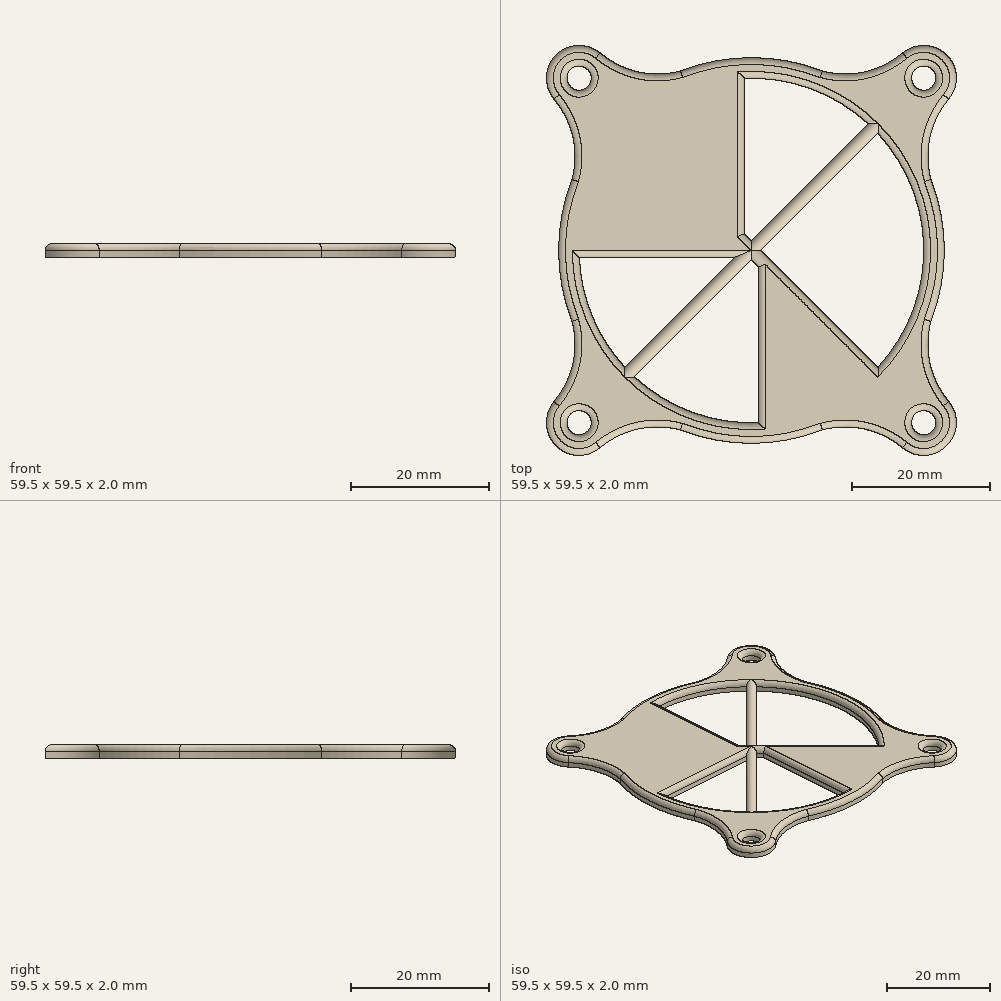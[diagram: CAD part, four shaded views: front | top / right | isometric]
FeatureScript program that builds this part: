
annotation { "Feature Type Name" : "Feature", "Feature Type Description" : "" }
export const myFeature = defineFeature(function(context is Context, id is Id, definition is map)
    precondition{}
    {
        {
            var Q0;
            Q0=qCreatedBy(makeId("Top.planeOp"),FACE);
            var sketch = newSketch(context, id + "F0", { "sketchPlane" : qUnion([Q0])});
            skCircle(sketch, "E0", {"center": v(0, 0) * mm, "radius": 25 * mm});
            skCircle(sketch, "E1.0", {"center": v(0, 0) * mm, "radius": 28 * mm});
            skLineSegment(sketch, "E2.bottom", {"start": v(25, 25) * mm, "end": v(-25, 25) * mm, "construction": true});
            skLineSegment(sketch, "E2.top", {"start": v(25, -25) * mm, "end": v(-25, -25) * mm, "construction": true});
            skLineSegment(sketch, "E2.left", {"start": v(25, 25) * mm, "end": v(25, -25) * mm, "construction": true});
            skLineSegment(sketch, "E2.right", {"start": v(-25, 25) * mm, "end": v(-25, -25) * mm, "construction": true});
            skCircle(sketch, "E3", {"center": v(-25, 25) * mm, "radius": 1.75 * mm});
            skCircle(sketch, "E4", {"center": v(25, 25) * mm, "radius": 1.75 * mm});
            skCircle(sketch, "E5", {"center": v(25, -25) * mm, "radius": 1.75 * mm});
            skCircle(sketch, "E6", {"center": v(-25, -25) * mm, "radius": 1.75 * mm});
            skCircle(sketch, "E7.0", {"center": v(-25, 25) * mm, "radius": 4.75 * mm});
            skCircle(sketch, "E8.0", {"center": v(25, 25) * mm, "radius": 4.75 * mm});
            skCircle(sketch, "E9.0", {"center": v(25, -25) * mm, "radius": 4.75 * mm});
            skCircle(sketch, "E10.0", {"center": v(-25, -25) * mm, "radius": 4.75 * mm});
            skLineSegment(sketch, "E11", {"start": v(0, 36.28) * mm, "end": v(0, -46.87) * mm, "construction": true});
            skLineSegment(sketch, "E12", {"start": v(-54.76, 0) * mm, "end": v(48.87, 0) * mm, "construction": true});
            skArc(sketch, "E13", {"start": v(26.04, -10.28) * mm, "mid": v(25.92, -16.43) * mm, "end": v(28.64, -21.95) * mm});
            skLineSegment(sketch, "E14", {"start": v(25, -25) * mm, "end": v(-25, 25) * mm, "construction": true});
            skArc(sketch, "E15.MirrorCS", {"start": v(10.28, -26.04) * mm, "mid": v(16.43, -25.92) * mm, "end": v(21.95, -28.64) * mm});
            skArc(sketch, "E16.MirrorCS", {"start": v(-26.04, -10.28) * mm, "mid": v(-25.92, -16.43) * mm, "end": v(-28.64, -21.95) * mm});
            skArc(sketch, "E17.MirrorCS", {"start": v(-10.28, -26.04) * mm, "mid": v(-16.43, -25.92) * mm, "end": v(-21.95, -28.64) * mm});
            skArc(sketch, "E18.MirrorCS", {"start": v(-26.04, 10.28) * mm, "mid": v(-25.92, 16.43) * mm, "end": v(-28.64, 21.95) * mm});
            skArc(sketch, "E19.MirrorCS", {"start": v(-10.28, 26.04) * mm, "mid": v(-16.43, 25.92) * mm, "end": v(-21.95, 28.64) * mm});
            skArc(sketch, "E20.MirrorCS", {"start": v(10.28, 26.04) * mm, "mid": v(16.43, 25.92) * mm, "end": v(21.95, 28.64) * mm});
            skArc(sketch, "E21.MirrorCS", {"start": v(26.04, 10.28) * mm, "mid": v(25.92, 16.43) * mm, "end": v(28.64, 21.95) * mm});
            skLineSegment(sketch, "E22", {"start": v(-24.98, -1) * mm, "end": v(25, -1) * mm});
            skLineSegment(sketch, "E23.MirrorCS", {"start": v(-24.98, 1) * mm, "end": v(25, 1) * mm});
            skLineSegment(sketch, "E24", {"start": v(1, -25) * mm, "end": v(1, 24.98) * mm});
            skLineSegment(sketch, "E25.MirrorCS", {"start": v(-1, -25) * mm, "end": v(-1, 24.98) * mm});
            skLineSegment(sketch, "E26", {"start": v(25, 25) * mm, "end": v(-25, -25) * mm, "construction": true});
            skLineSegment(sketch, "E27", {"start": v(16.96, 18.37) * mm, "end": v(-18.37, -16.96) * mm});
            skLineSegment(sketch, "E28.MirrorCS", {"start": v(18.37, 16.96) * mm, "end": v(-16.96, -18.37) * mm});
            skLineSegment(sketch, "E29", {"start": v(-18.37, 16.96) * mm, "end": v(16.96, -18.37) * mm});
            skLineSegment(sketch, "E30.MirrorCS", {"start": v(-16.96, 18.37) * mm, "end": v(18.37, -16.96) * mm});
            skSolve(sketch);
        }
        {
            var Q0;
            Q0 = qSketchRegion(id + "F0", true);
            var Q1;
            {var subQ0=sQuery(id+"F0.wireOp",EDGE,"E29");var subQ1=sQuery(id+"F0.wireOp",EDGE,"E0");var subQ2=makeQuery(id+"F0.imprint","INTERSECT",VERTEX,{"disambiguationData":[OD(0.0)],"derivedFrom":[subQ1,subQ0]});Q1=makeQuery(id+"F0.imprint","IMPRINT",FACE,{"disambiguationData":[TD([[makeQuery(id+"F0.imprint","IMPRINT",EDGE,{"disambiguationData":[TD([[subQ2,1.0]])],"derivedFrom":subQ1}),1.0]])]});}
            var Q2;
            {var subQ1=sQuery(id+"F0.wireOp",EDGE,"E0");var subQ5=sQuery(id+"F0.wireOp",EDGE,"E22");var subQ6=makeQuery(id+"F0.imprint","INTERSECT",VERTEX,{"disambiguationData":[OD(0.0)],"derivedFrom":[subQ1,subQ5]});Q2=makeQuery(id+"F0.imprint","IMPRINT",FACE,{"disambiguationData":[TD([[makeQuery(id+"F0.imprint","IMPRINT",EDGE,{"disambiguationData":[TD([[subQ6,1.0]])],"derivedFrom":subQ1}),1.0]])]});}
            var Q3;
            {var subQ0=sQuery(id+"F0.wireOp",EDGE,"E27");var subQ1=sQuery(id+"F0.wireOp",EDGE,"E0");var subQ2=makeQuery(id+"F0.imprint","INTERSECT",VERTEX,{"disambiguationData":[OD(0.0)],"derivedFrom":[subQ1,subQ0]});Q3=makeQuery(id+"F0.imprint","IMPRINT",FACE,{"disambiguationData":[TD([[makeQuery(id+"F0.imprint","IMPRINT",EDGE,{"disambiguationData":[TD([[subQ2,1.0]])],"derivedFrom":subQ1}),1.0]])]});}
            var Q4;
            {var subQ1=sQuery(id+"F0.wireOp",EDGE,"E0");var subQ5=sQuery(id+"F0.wireOp",EDGE,"E24");var subQ6=makeQuery(id+"F0.imprint","INTERSECT",VERTEX,{"disambiguationData":[OD(0.0)],"derivedFrom":[subQ1,subQ5]});Q4=makeQuery(id+"F0.imprint","IMPRINT",FACE,{"disambiguationData":[TD([[makeQuery(id+"F0.imprint","IMPRINT",EDGE,{"disambiguationData":[TD([[subQ6,-1.0]])],"derivedFrom":subQ1}),1.0]])]});}
            var Q5;
            {var subQ0=sQuery(id+"F0.wireOp",EDGE,"E27");var subQ1=sQuery(id+"F0.wireOp",EDGE,"E0");var subQ2=makeQuery(id+"F0.imprint","INTERSECT",VERTEX,{"disambiguationData":[OD(1.0)],"derivedFrom":[subQ1,subQ0]});Q5=makeQuery(id+"F0.imprint","IMPRINT",FACE,{"disambiguationData":[TD([[makeQuery(id+"F0.imprint","IMPRINT",EDGE,{"disambiguationData":[TD([[subQ2,-1.0]])],"derivedFrom":subQ1}),1.0]])]});}
            var Q6;
            {var subQ1=sQuery(id+"F0.wireOp",EDGE,"E25.MirrorCS");var subQ5=sQuery(id+"F0.wireOp",EDGE,"E0");var subQ6=makeQuery(id+"F0.imprint","INTERSECT",VERTEX,{"disambiguationData":[OD(1.0)],"derivedFrom":[subQ5,subQ1]});Q6=makeQuery(id+"F0.imprint","IMPRINT",FACE,{"disambiguationData":[TD([[makeQuery(id+"F0.imprint","IMPRINT",EDGE,{"disambiguationData":[TD([[subQ6,-1.0]])],"derivedFrom":subQ5}),1.0]])]});}
            var Q7;
            {var subQ0=sQuery(id+"F0.wireOp",EDGE,"E29");var subQ13=sQuery(id+"F0.wireOp",EDGE,"E22");var subQ14=makeQuery(id+"F0.imprint","INTERSECT",VERTEX,{"derivedFrom":[subQ13,subQ0]});Q7=makeQuery(id+"F0.imprint","IMPRINT",FACE,{"disambiguationData":[TD([[makeQuery(id+"F0.imprint","IMPRINT",EDGE,{"disambiguationData":[TD([[subQ14,-1.0]])],"derivedFrom":subQ13}),1.0]])]});}
            var Q8;
            {var subQ0=sQuery(id+"F0.wireOp",EDGE,"E29");var subQ1=sQuery(id+"F0.wireOp",EDGE,"E0");var subQ2=makeQuery(id+"F0.imprint","INTERSECT",VERTEX,{"disambiguationData":[OD(1.0)],"derivedFrom":[subQ1,subQ0]});Q8=makeQuery(id+"F0.imprint","IMPRINT",FACE,{"disambiguationData":[TD([[makeQuery(id+"F0.imprint","IMPRINT",EDGE,{"disambiguationData":[TD([[subQ2,-1.0]])],"derivedFrom":subQ1}),1.0]])]});}
            var Q9;
            {var subQ0=sQuery(id+"F0.wireOp",EDGE,"E23.MirrorCS");var subQ1=sQuery(id+"F0.wireOp",EDGE,"E0");var subQ2=makeQuery(id+"F0.imprint","INTERSECT",VERTEX,{"disambiguationData":[OD(1.0)],"derivedFrom":[subQ1,subQ0]});Q9=makeQuery(id+"F0.imprint","IMPRINT",FACE,{"disambiguationData":[TD([[makeQuery(id+"F0.imprint","IMPRINT",EDGE,{"disambiguationData":[TD([[subQ2,1.0]])],"derivedFrom":subQ1}),1.0]])]});}
            var Q10;
            {var subQ0=sQuery(id+"F0.wireOp",EDGE,"E24");var subQ1=sQuery(id+"F0.wireOp",EDGE,"E22");var subQ2=makeQuery(id+"F0.imprint","INTERSECT",VERTEX,{"derivedFrom":[subQ1,subQ0]});Q10=makeQuery(id+"F0.imprint","IMPRINT",FACE,{"disambiguationData":[TD([[makeQuery(id+"F0.imprint","IMPRINT",EDGE,{"disambiguationData":[TD([[subQ2,-1.0]])],"derivedFrom":subQ1}),1.0]])]});}
            var Q11;
            {var subQ0=sQuery(id+"F0.wireOp",EDGE,"E24");var subQ1=sQuery(id+"F0.wireOp",EDGE,"E23.MirrorCS");var subQ2=makeQuery(id+"F0.imprint","INTERSECT",VERTEX,{"derivedFrom":[subQ1,subQ0]});Q11=makeQuery(id+"F0.imprint","IMPRINT",FACE,{"disambiguationData":[TD([[makeQuery(id+"F0.imprint","IMPRINT",EDGE,{"disambiguationData":[TD([[subQ2,-1.0]])],"derivedFrom":subQ1}),-1.0]])]});}
            var Q12;
            {var subQ0=sQuery(id+"F0.wireOp",EDGE,"E25.MirrorCS");var subQ1=sQuery(id+"F0.wireOp",EDGE,"E23.MirrorCS");var subQ2=makeQuery(id+"F0.imprint","INTERSECT",VERTEX,{"derivedFrom":[subQ1,subQ0]});Q12=makeQuery(id+"F0.imprint","IMPRINT",FACE,{"disambiguationData":[TD([[makeQuery(id+"F0.imprint","IMPRINT",EDGE,{"disambiguationData":[TD([[subQ2,-1.0]])],"derivedFrom":subQ1}),1.0]])]});}
            var Q13;
            {var subQ0=sQuery(id+"F0.wireOp",EDGE,"E29");var subQ1=sQuery(id+"F0.wireOp",EDGE,"E23.MirrorCS");var subQ2=makeQuery(id+"F0.imprint","INTERSECT",VERTEX,{"derivedFrom":[subQ1,subQ0]});Q13=makeQuery(id+"F0.imprint","IMPRINT",FACE,{"disambiguationData":[TD([[makeQuery(id+"F0.imprint","IMPRINT",EDGE,{"disambiguationData":[TD([[subQ2,-1.0]])],"derivedFrom":subQ1}),-1.0]])]});}
            var Q14;
            {var subQ0=sQuery(id+"F0.wireOp",EDGE,"E30.MirrorCS");var subQ1=sQuery(id+"F0.wireOp",EDGE,"E23.MirrorCS");var subQ2=makeQuery(id+"F0.imprint","INTERSECT",VERTEX,{"derivedFrom":[subQ1,subQ0]});Q14=makeQuery(id+"F0.imprint","IMPRINT",FACE,{"disambiguationData":[TD([[makeQuery(id+"F0.imprint","IMPRINT",EDGE,{"disambiguationData":[TD([[subQ2,-1.0]])],"derivedFrom":subQ1}),1.0]])]});}
            var Q15;
            {var subQ0=sQuery(id+"F0.wireOp",EDGE,"E27");var subQ1=sQuery(id+"F0.wireOp",EDGE,"E22");var subQ2=makeQuery(id+"F0.imprint","INTERSECT",VERTEX,{"derivedFrom":[subQ1,subQ0]});Q15=makeQuery(id+"F0.imprint","IMPRINT",FACE,{"disambiguationData":[TD([[makeQuery(id+"F0.imprint","IMPRINT",EDGE,{"disambiguationData":[TD([[subQ2,-1.0]])],"derivedFrom":subQ1}),1.0]])]});}
            var Q16;
            {var subQ0=sQuery(id+"F0.wireOp",EDGE,"E25.MirrorCS");var subQ1=sQuery(id+"F0.wireOp",EDGE,"E22");var subQ2=makeQuery(id+"F0.imprint","INTERSECT",VERTEX,{"derivedFrom":[subQ1,subQ0]});Q16=makeQuery(id+"F0.imprint","IMPRINT",FACE,{"disambiguationData":[TD([[makeQuery(id+"F0.imprint","IMPRINT",EDGE,{"disambiguationData":[TD([[subQ2,-1.0]])],"derivedFrom":subQ1}),-1.0]])]});}
            var Q17;
            {var subQ0=sQuery(id+"F0.wireOp",EDGE,"E29");var subQ1=sQuery(id+"F0.wireOp",EDGE,"E22");var subQ2=makeQuery(id+"F0.imprint","INTERSECT",VERTEX,{"derivedFrom":[subQ1,subQ0]});Q17=makeQuery(id+"F0.imprint","IMPRINT",FACE,{"disambiguationData":[TD([[makeQuery(id+"F0.imprint","IMPRINT",EDGE,{"disambiguationData":[TD([[subQ2,-1.0]])],"derivedFrom":subQ1}),-1.0]])]});}
            var Q18;
            {var subQ0=sQuery(id+"F0.wireOp",EDGE,"E28.MirrorCS");var subQ1=sQuery(id+"F0.wireOp",EDGE,"E22");var subQ2=makeQuery(id+"F0.imprint","INTERSECT",VERTEX,{"derivedFrom":[subQ1,subQ0]});Q18=makeQuery(id+"F0.imprint","IMPRINT",FACE,{"disambiguationData":[TD([[makeQuery(id+"F0.imprint","IMPRINT",EDGE,{"disambiguationData":[TD([[subQ2,-1.0]])],"derivedFrom":subQ1}),1.0]])]});}
            var Q19;
            {var subQ0=sQuery(id+"F0.wireOp",EDGE,"E28.MirrorCS");var subQ1=sQuery(id+"F0.wireOp",EDGE,"E24");var subQ2=makeQuery(id+"F0.imprint","INTERSECT",VERTEX,{"derivedFrom":[subQ1,subQ0]});Q19=makeQuery(id+"F0.imprint","IMPRINT",FACE,{"disambiguationData":[TD([[makeQuery(id+"F0.imprint","IMPRINT",EDGE,{"disambiguationData":[TD([[subQ2,-1.0]])],"derivedFrom":subQ1}),-1.0]])]});}
            var Q20;
            {var subQ0=sQuery(id+"F0.wireOp",EDGE,"E30.MirrorCS");var subQ1=sQuery(id+"F0.wireOp",EDGE,"E23.MirrorCS");var subQ2=makeQuery(id+"F0.imprint","INTERSECT",VERTEX,{"derivedFrom":[subQ1,subQ0]});Q20=makeQuery(id+"F0.imprint","IMPRINT",FACE,{"disambiguationData":[TD([[makeQuery(id+"F0.imprint","IMPRINT",EDGE,{"disambiguationData":[TD([[subQ2,-1.0]])],"derivedFrom":subQ1}),-1.0]])]});}
            var Q21;
            {var subQ0=sQuery(id+"F0.wireOp",EDGE,"E27");var subQ1=sQuery(id+"F0.wireOp",EDGE,"E23.MirrorCS");var subQ2=makeQuery(id+"F0.imprint","INTERSECT",VERTEX,{"derivedFrom":[subQ1,subQ0]});Q21=makeQuery(id+"F0.imprint","IMPRINT",FACE,{"disambiguationData":[TD([[makeQuery(id+"F0.imprint","IMPRINT",EDGE,{"disambiguationData":[TD([[subQ2,-1.0]])],"derivedFrom":subQ1}),1.0]])]});}
            var Q22;
            {var subQ0=sQuery(id+"F0.wireOp",EDGE,"E25.MirrorCS");var subQ1=sQuery(id+"F0.wireOp",EDGE,"E23.MirrorCS");var subQ2=makeQuery(id+"F0.imprint","INTERSECT",VERTEX,{"derivedFrom":[subQ1,subQ0]});Q22=makeQuery(id+"F0.imprint","IMPRINT",FACE,{"disambiguationData":[TD([[makeQuery(id+"F0.imprint","IMPRINT",EDGE,{"disambiguationData":[TD([[subQ2,-1.0]])],"derivedFrom":subQ1}),-1.0]])]});}
            var Q23;
            {var subQ0=sQuery(id+"F0.wireOp",EDGE,"E29");var subQ1=sQuery(id+"F0.wireOp",EDGE,"E25.MirrorCS");var subQ2=makeQuery(id+"F0.imprint","INTERSECT",VERTEX,{"derivedFrom":[subQ1,subQ0]});Q23=makeQuery(id+"F0.imprint","IMPRINT",FACE,{"disambiguationData":[TD([[makeQuery(id+"F0.imprint","IMPRINT",EDGE,{"disambiguationData":[TD([[subQ2,-1.0]])],"derivedFrom":subQ1}),1.0]])]});}
            var Q24;
            {var subQ0=sQuery(id+"F0.wireOp",EDGE,"E25.MirrorCS");var subQ1=sQuery(id+"F0.wireOp",EDGE,"E22");var subQ2=makeQuery(id+"F0.imprint","INTERSECT",VERTEX,{"derivedFrom":[subQ1,subQ0]});Q24=makeQuery(id+"F0.imprint","IMPRINT",FACE,{"disambiguationData":[TD([[makeQuery(id+"F0.imprint","IMPRINT",EDGE,{"disambiguationData":[TD([[subQ2,-1.0]])],"derivedFrom":subQ1}),1.0]])]});}
            var Q25;
            {var subQ0=sQuery(id+"F0.wireOp",EDGE,"E28.MirrorCS");var subQ1=sQuery(id+"F0.wireOp",EDGE,"E22");var subQ2=makeQuery(id+"F0.imprint","INTERSECT",VERTEX,{"derivedFrom":[subQ1,subQ0]});Q25=makeQuery(id+"F0.imprint","IMPRINT",FACE,{"disambiguationData":[TD([[makeQuery(id+"F0.imprint","IMPRINT",EDGE,{"disambiguationData":[TD([[subQ2,-1.0]])],"derivedFrom":subQ1}),-1.0]])]});}
            extrude(context, id + "F1", {"entities" : qUnion([Q0, Q1, Q2, Q3, Q4, Q5, Q6, Q7, Q8, Q9, Q10, Q11, Q12, Q13, Q14, Q15, Q16, Q17, Q18, Q19, Q20, Q21, Q22, Q23, Q24, Q25]), "depth" : 2 * mm});
        }
        {
            var Q0;
            Q0=makeQuery(id+"F1.opExtrude","CAP_FACE",FACE,{"disambiguationData":[OSD([sQuery(id+"F0.wireOp",EDGE,"E0"),sQuery(id+"F0.wireOp",EDGE,"E1.0"),sQuery(id+"F0.wireOp",EDGE,"E3"),sQuery(id+"F0.wireOp",EDGE,"E4"),sQuery(id+"F0.wireOp",EDGE,"E5"),sQuery(id+"F0.wireOp",EDGE,"E6"),sQuery(id+"F0.wireOp",EDGE,"E7.0"),sQuery(id+"F0.wireOp",EDGE,"E8.0"),sQuery(id+"F0.wireOp",EDGE,"E9.0"),sQuery(id+"F0.wireOp",EDGE,"E10.0"),sQuery(id+"F0.wireOp",EDGE,"E13"),sQuery(id+"F0.wireOp",EDGE,"E15.MirrorCS"),sQuery(id+"F0.wireOp",EDGE,"E16.MirrorCS"),sQuery(id+"F0.wireOp",EDGE,"E17.MirrorCS"),sQuery(id+"F0.wireOp",EDGE,"E18.MirrorCS"),sQuery(id+"F0.wireOp",EDGE,"E19.MirrorCS"),sQuery(id+"F0.wireOp",EDGE,"E20.MirrorCS"),sQuery(id+"F0.wireOp",EDGE,"E21.MirrorCS"),sQuery(id+"F0.wireOp",EDGE,"E22"),sQuery(id+"F0.wireOp",EDGE,"E23.MirrorCS"),sQuery(id+"F0.wireOp",EDGE,"E24"),sQuery(id+"F0.wireOp",EDGE,"E25.MirrorCS"),sQuery(id+"F0.wireOp",EDGE,"E27"),sQuery(id+"F0.wireOp",EDGE,"E28.MirrorCS"),sQuery(id+"F0.wireOp",EDGE,"E29"),sQuery(id+"F0.wireOp",EDGE,"E30.MirrorCS")])],"isStart":false});
            fillet(context, id + "F2", {"entities" : qUnion([Q0]), "radius" : 1 * mm, "tangentPropagation" : true, "allowEdgeOverflow" : false});
        }
    });
